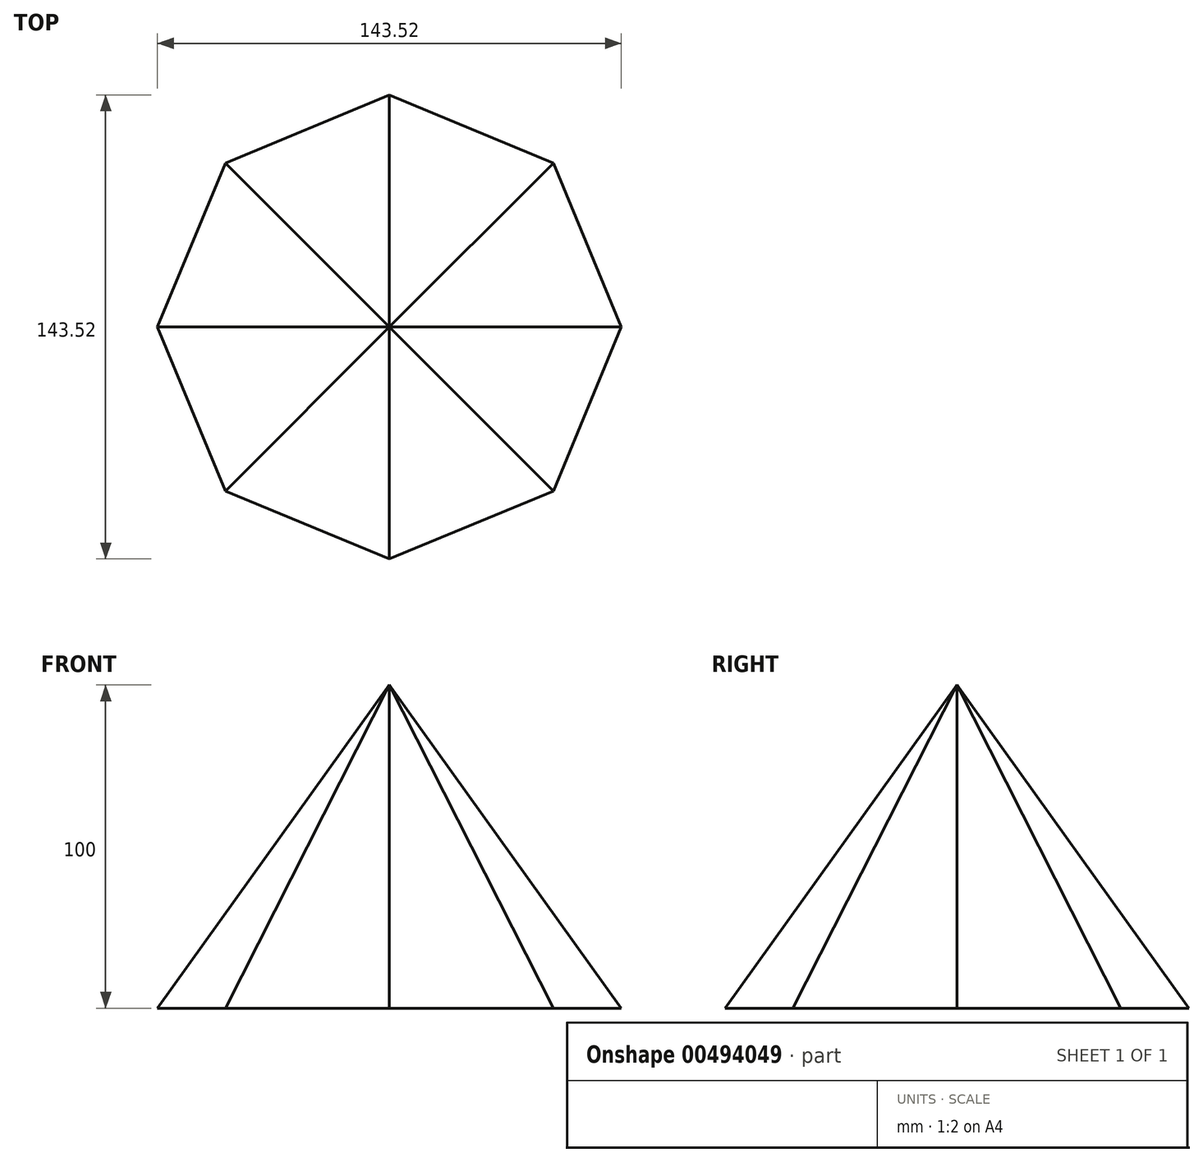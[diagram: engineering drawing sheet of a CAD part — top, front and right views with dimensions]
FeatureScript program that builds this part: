
annotation { "Feature Type Name" : "Feature", "Feature Type Description" : "" }
export const myFeature = defineFeature(function(context is Context, id is Id, definition is map)
    precondition{}
    {
        {
            var Q0;
            Q0=qCreatedBy(makeId("Top.planeOp"),FACE);
            var sketch = newSketch(context, id + "F0", { "sketchPlane" : qUnion([Q0])});
            skCircle(sketch, "E0.cCircle", {"center": v(0, 0) * mm, "radius": 71.76 * mm, "construction": true});
            skLineSegment(sketch, "E0.0", {"start": v(0, 71.76) * mm, "end": v(50.74, 50.74) * mm});
            skLineSegment(sketch, "E0.1", {"start": v(50.74, 50.74) * mm, "end": v(71.76, 0) * mm});
            skLineSegment(sketch, "E0.2", {"start": v(71.76, 0) * mm, "end": v(50.74, -50.74) * mm});
            skLineSegment(sketch, "E0.3", {"start": v(50.74, -50.74) * mm, "end": v(0, -71.76) * mm});
            skLineSegment(sketch, "E0.4", {"start": v(0, -71.76) * mm, "end": v(-50.74, -50.74) * mm});
            skLineSegment(sketch, "E0.5", {"start": v(-50.74, -50.74) * mm, "end": v(-71.76, 0) * mm});
            skLineSegment(sketch, "E0.6", {"start": v(-71.76, 0) * mm, "end": v(-50.74, 50.74) * mm});
            skLineSegment(sketch, "E0.7", {"start": v(-50.74, 50.74) * mm, "end": v(0, 71.76) * mm});
            skSolve(sketch);
        }
        {
            var Q0;
            Q0=qCreatedBy(makeId("Top.planeOp"),FACE);
            cPlane(context, id + "F1", {"entities" : qUnion([Q0]), "cplaneType" : CPlaneType.OFFSET, "offset" : 100 * mm, "width" : 150 * mm, "height" : 150 * mm});
        }
        {
            var Q0;
            Q0=qCreatedBy(id+"F1.planeOp",FACE);
            var sketch = newSketch(context, id + "F2", { "sketchPlane" : qUnion([Q0])});
            skPoint(sketch, "E1", {"position": v(0, 0) * mm});
            skSolve(sketch);
        }
        {
            var Q0;
            Q0=sQuery(id+"F2.wireOp",VERTEX,"E1");
            var Q1;
            Q1=makeQuery(id+"F0.imprint","IMPRINT",FACE,{"disambiguationData":[TD([[makeQuery(id+"F0.imprint","IMPRINT",EDGE,{"derivedFrom":sQuery(id+"F0.wireOp",EDGE,"E0.0")}),-1.0]])]});
            loft(context, id + "F3", {"sheetProfilesArray" : [{ "sheetProfileEntities" : qUnion([Q0]) }, { "sheetProfileEntities" : qUnion([Q1]) }]});
        }
    });
